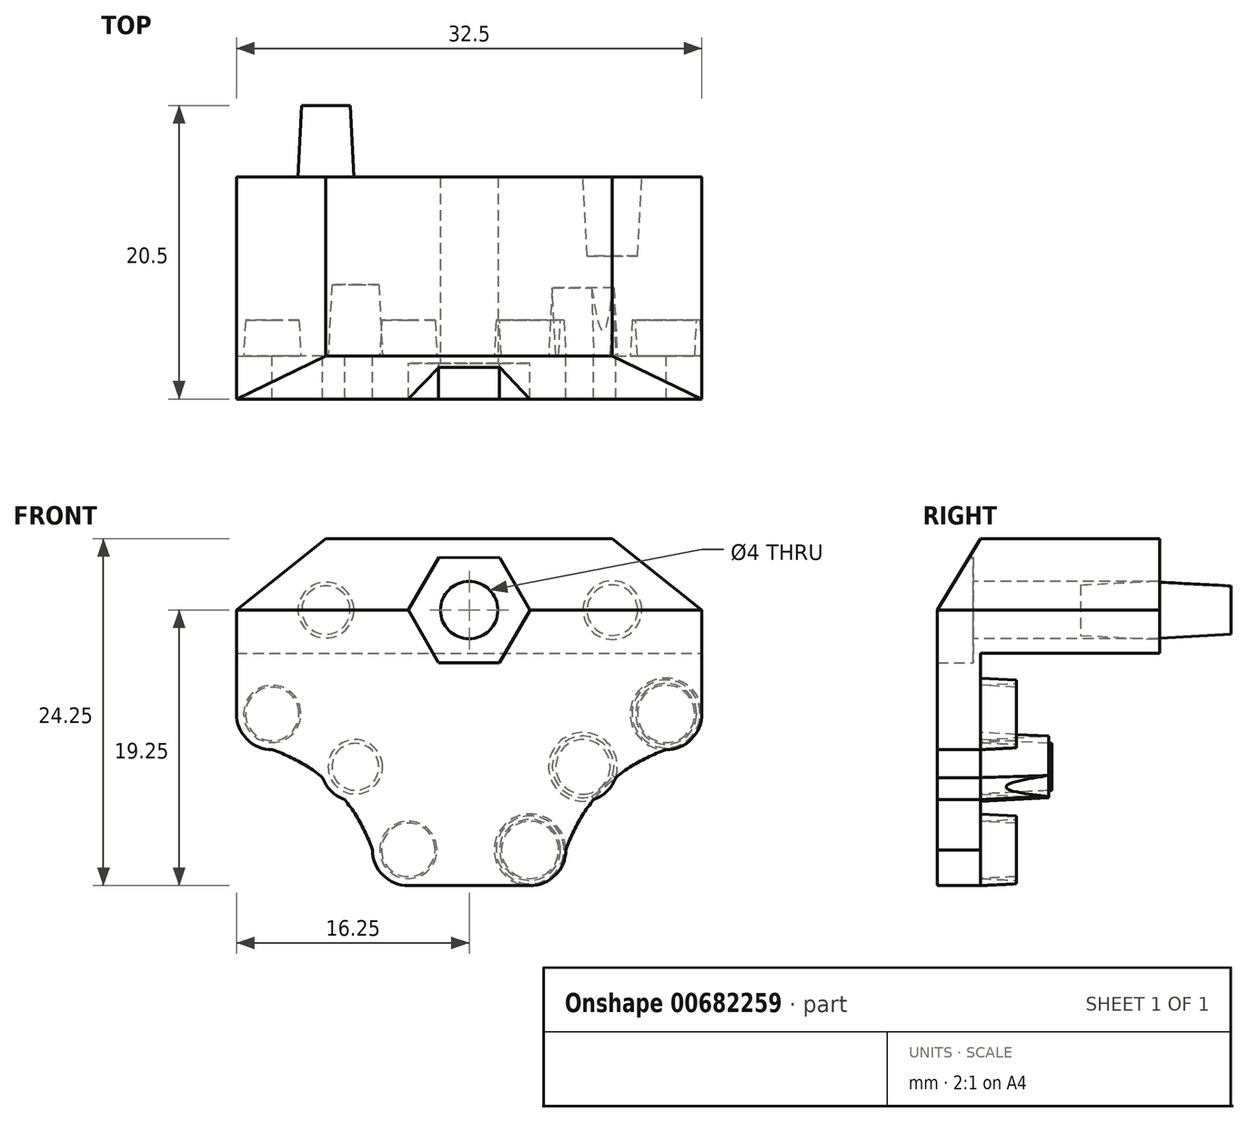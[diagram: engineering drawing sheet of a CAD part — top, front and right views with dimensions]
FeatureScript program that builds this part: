
annotation { "Feature Type Name" : "Feature", "Feature Type Description" : "" }
export const myFeature = defineFeature(function(context is Context, id is Id, definition is map)
    precondition{}
    {
        {
            var Q0;
            Q0=qCreatedBy(makeId("Front.planeOp"),FACE);
            var sketch = newSketch(context, id + "F0", { "sketchPlane" : qUnion([Q0])});
            skLineSegment(sketch, "E0", {"start": v(0, 0) * mm, "end": v(-4.25, 0) * mm});
            skLineSegment(sketch, "E1", {"start": v(0, 0) * mm, "end": v(0, -4.25) * mm});
            skLineSegment(sketch, "E2", {"start": v(0, 0) * mm, "end": v(0, -7.95) * mm});
            skLineSegment(sketch, "E3", {"start": v(0, 0) * mm, "end": v(-7.95, 0) * mm});
            skLineSegment(sketch, "E4", {"start": v(0, 0) * mm, "end": v(0, -13.75) * mm});
            skLineSegment(sketch, "E5", {"start": v(0, 0) * mm, "end": v(-13.75, 0) * mm});
            skCircle(sketch, "E6", {"center": v(-4.25, -13.75) * mm, "radius": 2 * mm});
            skCircle(sketch, "E7", {"center": v(-13.75, -4.25) * mm, "radius": 2 * mm});
            skCircle(sketch, "E8", {"center": v(-7.95, -7.95) * mm, "radius": 1.9 * mm});
            skLineSegment(sketch, "E9", {"start": v(0, 0) * mm, "end": v(0, 3) * mm});
            skCircle(sketch, "E10", {"center": v(0, 3) * mm, "radius": 2 * mm});
            skCircle(sketch, "E11.cCircle", {"center": v(0, 3) * mm, "radius": 4.25 * mm, "construction": true});
            skLineSegment(sketch, "E11.0", {"start": v(2.15, 6.67) * mm, "end": v(4.25, 2.97) * mm});
            skLineSegment(sketch, "E11.1", {"start": v(4.25, 2.97) * mm, "end": v(2.1, -0.7) * mm});
            skLineSegment(sketch, "E11.2", {"start": v(2.1, -0.7) * mm, "end": v(-2.15, -0.67) * mm});
            skLineSegment(sketch, "E11.3", {"start": v(-2.15, -0.67) * mm, "end": v(-4.25, 3.03) * mm});
            skLineSegment(sketch, "E11.4", {"start": v(-4.25, 3.03) * mm, "end": v(-2.1, 6.7) * mm});
            skLineSegment(sketch, "E11.5", {"start": v(-2.1, 6.7) * mm, "end": v(2.15, 6.67) * mm});
            skCircle(sketch, "E12.MirrorC", {"center": v(4.25, -13.75) * mm, "radius": 2 * mm});
            skCircle(sketch, "E13.MirrorC", {"center": v(7.95, -7.95) * mm, "radius": 1.9 * mm});
            skCircle(sketch, "E14.MirrorC", {"center": v(13.75, -4.25) * mm, "radius": 2 * mm});
            skLineSegment(sketch, "E15", {"start": v(0, 0) * mm, "end": v(0, 12) * mm});
            skCircle(sketch, "E16", {"center": v(-13.75, -4.25) * mm, "radius": 2.5 * mm});
            skCircle(sketch, "E17", {"center": v(-7.95, -7.95) * mm, "radius": 2.4 * mm});
            skCircle(sketch, "E18", {"center": v(-4.25, -13.75) * mm, "radius": 2.5 * mm});
            skLineSegment(sketch, "E19", {"start": v(-4.25, -16.25) * mm, "end": v(0, -16.25) * mm});
            skLineSegment(sketch, "E20", {"start": v(-16.25, -4.25) * mm, "end": v(-16.25, 0) * mm});
            skLineSegment(sketch, "E21", {"start": v(-16.25, 0) * mm, "end": v(-16.25, 3) * mm});
            skLineSegment(sketch, "E22", {"start": v(-16.25, 3) * mm, "end": v(-10, 8) * mm});
            skLineSegment(sketch, "E23", {"start": v(-10, 8) * mm, "end": v(0, 8) * mm});
            skLineSegment(sketch, "E24.MirrorCS", {"start": v(10, 8) * mm, "end": v(0, 8) * mm});
            skLineSegment(sketch, "E25.MirrorCS", {"start": v(16.25, 3) * mm, "end": v(10, 8) * mm});
            skLineSegment(sketch, "E26.MirrorCS", {"start": v(16.25, 0) * mm, "end": v(16.25, 3) * mm});
            skLineSegment(sketch, "E27.MirrorCS", {"start": v(16.25, -4.25) * mm, "end": v(16.25, 0) * mm});
            skCircle(sketch, "E28.MirrorC", {"center": v(13.75, -4.25) * mm, "radius": 2.5 * mm});
            skCircle(sketch, "E29.MirrorC", {"center": v(4.25, -13.75) * mm, "radius": 2.5 * mm});
            skLineSegment(sketch, "E30.MirrorCS", {"start": v(4.25, -16.25) * mm, "end": v(0, -16.25) * mm});
            skFitSpline(sketch, "E31", {"points": [v(-6.75, -13.75) * mm, v(-13.75, -6.75) * mm], "startDerivative": vector(-3.6, 10.2) * mm, "endDerivative": vector(-10.2, 3.6) * mm});
            skFitSpline(sketch, "E32.MirrorCS", {"points": [v(6.75, -13.75) * mm, v(13.75, -6.75) * mm], "startDerivative": vector(3.6, 10.2) * mm, "endDerivative": vector(10.2, 3.6) * mm});
            skCircle(sketch, "E33.MirrorC", {"center": v(7.95, -7.95) * mm, "radius": 2.4 * mm});
            skLineSegment(sketch, "E34", {"start": v(-16.25, 0) * mm, "end": v(16.25, 0) * mm});
            skSolve(sketch);
        }
        {
            var Q0;
            {var subQ7=sQuery(id+"F0.wireOp",EDGE,"E11.4");Q0=makeQuery(id+"F0.imprint","IMPRINT",FACE,{"disambiguationData":[TD([[makeQuery(id+"F0.imprint","IMPRINT",EDGE,{"derivedFrom":subQ7}),1.0]])]});}
            var Q1;
            {var subQ4=sQuery(id+"F0.wireOp",EDGE,"E11.0");Q1=makeQuery(id+"F0.imprint","IMPRINT",FACE,{"disambiguationData":[TD([[makeQuery(id+"F0.imprint","IMPRINT",EDGE,{"derivedFrom":subQ4}),1.0]])]});}
            var Q2;
            {var subQ31=sQuery(id+"F0.wireOp",EDGE,"E19");Q2=makeQuery(id+"F0.imprint","IMPRINT",FACE,{"disambiguationData":[TD([[makeQuery(id+"F0.imprint","IMPRINT",EDGE,{"derivedFrom":subQ31}),1.0]])]});}
            var Q3;
            {var subQ0=sQuery(id+"F0.wireOp",EDGE,"E31");var subQ1=sQuery(id+"F0.wireOp",EDGE,"E17");var subQ2=makeQuery(id+"F0.imprint","INTERSECT",VERTEX,{"disambiguationData":[OD(0.0)],"derivedFrom":[subQ1,subQ0]});Q3=makeQuery(id+"F0.imprint","IMPRINT",FACE,{"disambiguationData":[TD([[makeQuery(id+"F0.imprint","IMPRINT",EDGE,{"disambiguationData":[TD([[subQ2,1.0]])],"derivedFrom":subQ1}),1.0]])]});}
            var Q4;
            Q4=makeQuery(id+"F0.imprint","IMPRINT",FACE,{"disambiguationData":[TD([[makeQuery(id+"F0.imprint","IMPRINT",EDGE,{"derivedFrom":sQuery(id+"F0.wireOp",EDGE,"E8")}),-1.0]])]});
            var Q5;
            Q5=makeQuery(id+"F0.imprint","IMPRINT",FACE,{"disambiguationData":[TD([[makeQuery(id+"F0.imprint","IMPRINT",EDGE,{"derivedFrom":sQuery(id+"F0.wireOp",EDGE,"E8")}),1.0]])]});
            var Q6;
            Q6=makeQuery(id+"F0.imprint","IMPRINT",FACE,{"disambiguationData":[TD([[makeQuery(id+"F0.imprint","IMPRINT",EDGE,{"derivedFrom":sQuery(id+"F0.wireOp",EDGE,"E7")}),-1.0]])]});
            var Q7;
            Q7=makeQuery(id+"F0.imprint","IMPRINT",FACE,{"disambiguationData":[TD([[makeQuery(id+"F0.imprint","IMPRINT",EDGE,{"derivedFrom":sQuery(id+"F0.wireOp",EDGE,"E7")}),1.0]])]});
            var Q8;
            Q8=makeQuery(id+"F0.imprint","IMPRINT",FACE,{"disambiguationData":[TD([[makeQuery(id+"F0.imprint","IMPRINT",EDGE,{"derivedFrom":sQuery(id+"F0.wireOp",EDGE,"E6")}),1.0]])]});
            var Q9;
            Q9=makeQuery(id+"F0.imprint","IMPRINT",FACE,{"disambiguationData":[TD([[makeQuery(id+"F0.imprint","IMPRINT",EDGE,{"derivedFrom":sQuery(id+"F0.wireOp",EDGE,"E6")}),-1.0]])]});
            var Q10;
            Q10=makeQuery(id+"F0.imprint","IMPRINT",FACE,{"disambiguationData":[TD([[makeQuery(id+"F0.imprint","IMPRINT",EDGE,{"derivedFrom":sQuery(id+"F0.wireOp",EDGE,"E12.MirrorC")}),-1.0]])]});
            var Q11;
            Q11=makeQuery(id+"F0.imprint","IMPRINT",FACE,{"disambiguationData":[TD([[makeQuery(id+"F0.imprint","IMPRINT",EDGE,{"derivedFrom":sQuery(id+"F0.wireOp",EDGE,"E12.MirrorC")}),1.0]])]});
            var Q12;
            {var subQ0=sQuery(id+"F0.wireOp",EDGE,"E33.MirrorC");var subQ1=sQuery(id+"F0.wireOp",EDGE,"E32.MirrorCS");var subQ2=makeQuery(id+"F0.imprint","INTERSECT",VERTEX,{"disambiguationData":[OD(0.0)],"derivedFrom":[subQ1,subQ0]});Q12=makeQuery(id+"F0.imprint","IMPRINT",FACE,{"disambiguationData":[TD([[makeQuery(id+"F0.imprint","IMPRINT",EDGE,{"disambiguationData":[TD([[subQ2,-1.0]])],"derivedFrom":subQ1}),-1.0]])]});}
            var Q13;
            Q13=makeQuery(id+"F0.imprint","IMPRINT",FACE,{"disambiguationData":[TD([[makeQuery(id+"F0.imprint","IMPRINT",EDGE,{"derivedFrom":sQuery(id+"F0.wireOp",EDGE,"E13.MirrorC")}),1.0]])]});
            var Q14;
            Q14=makeQuery(id+"F0.imprint","IMPRINT",FACE,{"disambiguationData":[TD([[makeQuery(id+"F0.imprint","IMPRINT",EDGE,{"derivedFrom":sQuery(id+"F0.wireOp",EDGE,"E13.MirrorC")}),-1.0]])]});
            var Q15;
            Q15=makeQuery(id+"F0.imprint","IMPRINT",FACE,{"disambiguationData":[TD([[makeQuery(id+"F0.imprint","IMPRINT",EDGE,{"derivedFrom":sQuery(id+"F0.wireOp",EDGE,"E14.MirrorC")}),1.0]])]});
            var Q16;
            Q16=makeQuery(id+"F0.imprint","IMPRINT",FACE,{"disambiguationData":[TD([[makeQuery(id+"F0.imprint","IMPRINT",EDGE,{"derivedFrom":sQuery(id+"F0.wireOp",EDGE,"E14.MirrorC")}),-1.0]])]});
            extrude(context, id + "F1", {"entities" : qUnion([Q0, Q1, Q2, Q3, Q4, Q5, Q6, Q7, Q8, Q9, Q10, Q11, Q12, Q13, Q14, Q15, Q16]), "depth" : 3 * mm, "offsetDistance" : 25 * mm});
        }
        {
            var Q0;
            Q0=makeQuery(id+"F0.imprint","IMPRINT",FACE,{"disambiguationData":[TD([[makeQuery(id+"F0.imprint","IMPRINT",EDGE,{"derivedFrom":sQuery(id+"F0.wireOp",EDGE,"E8")}),1.0]])]});
            var Q1;
            Q1=makeQuery(id+"F0.imprint","IMPRINT",FACE,{"disambiguationData":[TD([[makeQuery(id+"F0.imprint","IMPRINT",EDGE,{"derivedFrom":sQuery(id+"F0.wireOp",EDGE,"E13.MirrorC")}),-1.0]])]});
            extrude(context, id + "F2", {"entities" : qUnion([Q0, Q1]), "operationType" : NewBodyOperationType.ADD, "oppositeDirection" : true, "depth" : 5 * mm, "offsetDistance" : 25 * mm, "hasDraft" : true, "draftAngle" : 3 * degree, "draftPullDirection" : true});
        }
        {
            var Q0;
            {var subQ7=sQuery(id+"F0.wireOp",EDGE,"E11.4");Q0=makeQuery(id+"F0.imprint","IMPRINT",FACE,{"disambiguationData":[TD([[makeQuery(id+"F0.imprint","IMPRINT",EDGE,{"derivedFrom":subQ7}),1.0]])]});}
            var Q1;
            {var subQ4=sQuery(id+"F0.wireOp",EDGE,"E11.0");Q1=makeQuery(id+"F0.imprint","IMPRINT",FACE,{"disambiguationData":[TD([[makeQuery(id+"F0.imprint","IMPRINT",EDGE,{"derivedFrom":subQ4}),1.0]])]});}
            var Q2;
            {var subQ1=sQuery(id+"F0.wireOp",EDGE,"E11.0");Q2=makeQuery(id+"F0.imprint","IMPRINT",FACE,{"disambiguationData":[TD([[makeQuery(id+"F0.imprint","IMPRINT",EDGE,{"derivedFrom":subQ1}),-1.0]])]});}
            var Q3;
            {var subQ0=sQuery(id+"F0.wireOp",EDGE,"E11.4");Q3=makeQuery(id+"F0.imprint","IMPRINT",FACE,{"disambiguationData":[TD([[makeQuery(id+"F0.imprint","IMPRINT",EDGE,{"derivedFrom":subQ0}),-1.0]])]});}
            extrude(context, id + "F3", {"entities" : qUnion([Q0, Q1, Q2, Q3]), "operationType" : NewBodyOperationType.ADD, "oppositeDirection" : true, "depth" : 12.5 * mm, "offsetDistance" : 25 * mm});
        }
        {
            var Q0;
            Q0=makeQuery(id+"F1.opExtrude","CAP_EDGE",EDGE,{"disambiguationData":[OSD([sQuery(id+"F0.wireOp",EDGE,"E23"),sQuery(id+"F0.wireOp",EDGE,"E24.MirrorCS")])],"isStart":false});
            chamfer(context, id + "F4", {"entities" : qUnion([Q0]), "chamferType" : ChamferType.TWO_OFFSETS, "width1" : 3 * mm, "oppositeDirection" : false, "width2" : 5 * mm, "tangentPropagation" : true});
        }
        {
            var Q0;
            Q0=makeQuery(id+"F0.imprint","IMPRINT",FACE,{"disambiguationData":[TD([[makeQuery(id+"F0.imprint","IMPRINT",EDGE,{"derivedFrom":sQuery(id+"F0.wireOp",EDGE,"E14.MirrorC")}),-1.0]])]});
            var Q1;
            Q1=makeQuery(id+"F0.imprint","IMPRINT",FACE,{"disambiguationData":[TD([[makeQuery(id+"F0.imprint","IMPRINT",EDGE,{"derivedFrom":sQuery(id+"F0.wireOp",EDGE,"E12.MirrorC")}),-1.0]])]});
            var Q2;
            Q2=makeQuery(id+"F0.imprint","IMPRINT",FACE,{"disambiguationData":[TD([[makeQuery(id+"F0.imprint","IMPRINT",EDGE,{"derivedFrom":sQuery(id+"F0.wireOp",EDGE,"E6")}),1.0]])]});
            var Q3;
            Q3=makeQuery(id+"F0.imprint","IMPRINT",FACE,{"disambiguationData":[TD([[makeQuery(id+"F0.imprint","IMPRINT",EDGE,{"derivedFrom":sQuery(id+"F0.wireOp",EDGE,"E7")}),1.0]])]});
            extrude(context, id + "F5", {"entities" : qUnion([Q0, Q1, Q2, Q3]), "operationType" : NewBodyOperationType.ADD, "oppositeDirection" : true, "depth" : 2.5 * mm, "offsetDistance" : 25 * mm, "hasDraft" : true, "draftAngle" : 3 * degree, "draftPullDirection" : true});
        }
        {
            var Q0;
            Q0=makeQuery(id+"F3.opExtrude","CAP_FACE",FACE,{"disambiguationData":[OSD([sQuery(id+"F0.wireOp",EDGE,"E10"),sQuery(id+"F0.wireOp",EDGE,"E21"),sQuery(id+"F0.wireOp",EDGE,"E22"),sQuery(id+"F0.wireOp",EDGE,"E23"),sQuery(id+"F0.wireOp",EDGE,"E24.MirrorCS"),sQuery(id+"F0.wireOp",EDGE,"E25.MirrorCS"),sQuery(id+"F0.wireOp",EDGE,"E26.MirrorCS"),sQuery(id+"F0.wireOp",EDGE,"E34")])],"isStart":false});
            var sketch = newSketch(context, id + "F6", { "sketchPlane" : qUnion([Q0])});
            skLineSegment(sketch, "E35", {"start": v(0, 0) * mm, "end": v(0, 3) * mm});
            skLineSegment(sketch, "E36", {"start": v(0, 3) * mm, "end": v(10, 3) * mm});
            skLineSegment(sketch, "E37", {"start": v(0, 3) * mm, "end": v(-10, 3) * mm});
            skCircle(sketch, "E38", {"center": v(-10, 3) * mm, "radius": 2.05 * mm});
            skCircle(sketch, "E39", {"center": v(10, 3) * mm, "radius": 1.95 * mm});
            skSolve(sketch);
        }
        {
            var Q0;
            Q0=makeQuery(id+"F6.imprint","IMPRINT",FACE,{"disambiguationData":[TD([[makeQuery(id+"F6.imprint","IMPRINT",EDGE,{"derivedFrom":sQuery(id+"F6.wireOp",EDGE,"E39")}),1.0]])]});
            extrude(context, id + "F7", {"entities" : qUnion([Q0]), "operationType" : NewBodyOperationType.ADD, "depth" : 5 * mm, "offsetDistance" : 25 * mm, "hasDraft" : true, "draftAngle" : 3 * degree, "draftPullDirection" : true});
        }
        {
            var Q0;
            Q0=makeQuery(id+"F6.imprint","IMPRINT",FACE,{"disambiguationData":[TD([[makeQuery(id+"F6.imprint","IMPRINT",EDGE,{"derivedFrom":sQuery(id+"F6.wireOp",EDGE,"E38")}),1.0]])]});
            extrude(context, id + "F8", {"entities" : qUnion([Q0]), "operationType" : NewBodyOperationType.REMOVE, "oppositeDirection" : true, "depth" : 5.5 * mm, "offsetDistance" : 25 * mm, "hasDraft" : true, "draftAngle" : 3 * degree, "draftPullDirection" : true});
        }
        {
            var Q0;
            {var subQ3=sQuery(id+"F0.wireOp",EDGE,"E11.2");var subQ5=sQuery(id+"F0.wireOp",EDGE,"E11.3");var subQ6=makeQuery(id+"F0.imprint","INTERSECT",VERTEX,{"derivedFrom":[subQ3,subQ5]});Q0=makeQuery(id+"F0.imprint","IMPRINT",FACE,{"disambiguationData":[TD([[makeQuery(id+"F0.imprint","IMPRINT",EDGE,{"disambiguationData":[TD([[subQ6,1.0]])],"derivedFrom":subQ3}),-1.0]])]});}
            var Q1;
            {var subQ3=sQuery(id+"F0.wireOp",EDGE,"E11.2");var subQ5=sQuery(id+"F0.wireOp",EDGE,"E11.1");var subQ6=makeQuery(id+"F0.imprint","INTERSECT",VERTEX,{"derivedFrom":[subQ5,subQ3]});Q1=makeQuery(id+"F0.imprint","IMPRINT",FACE,{"disambiguationData":[TD([[makeQuery(id+"F0.imprint","IMPRINT",EDGE,{"disambiguationData":[TD([[subQ6,1.0]])],"derivedFrom":subQ5}),-1.0]])]});}
            var Q2;
            {var subQ1=sQuery(id+"F0.wireOp",EDGE,"E11.0");Q2=makeQuery(id+"F0.imprint","IMPRINT",FACE,{"disambiguationData":[TD([[makeQuery(id+"F0.imprint","IMPRINT",EDGE,{"derivedFrom":subQ1}),-1.0]])]});}
            var Q3;
            {var subQ0=sQuery(id+"F0.wireOp",EDGE,"E11.4");Q3=makeQuery(id+"F0.imprint","IMPRINT",FACE,{"disambiguationData":[TD([[makeQuery(id+"F0.imprint","IMPRINT",EDGE,{"derivedFrom":subQ0}),-1.0]])]});}
            extrude(context, id + "F9", {"entities" : qUnion([Q0, Q1, Q2, Q3]), "operationType" : NewBodyOperationType.ADD, "depth" : 0.5 * mm, "offsetDistance" : 25 * mm});
        }
    });
